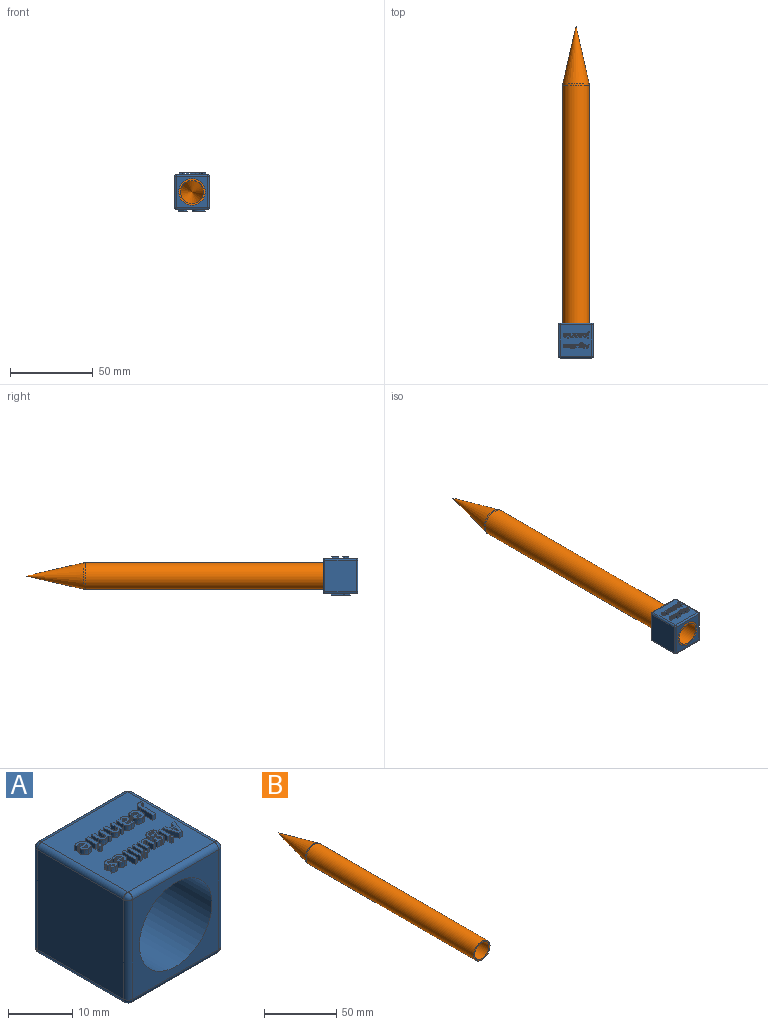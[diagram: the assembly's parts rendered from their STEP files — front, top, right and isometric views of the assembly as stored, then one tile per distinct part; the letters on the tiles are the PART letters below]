
ASSEMBLY  parts=2 mates=1
PART A: 354 faces, bbox 21x21x23 mm
  f0: plane 19x19mm, normal (0,0,1), area 317.9mm2, adj f7,f8,f9,f10,f11,f12,f13,f14
  f1: plane 19x19mm, normal (0,0,-1), area 267.5mm2, adj f136,f140,f141,f142,f156,f157,f158,f159
  f2: plane 19x19mm, normal (-1,0,0), area 361mm2, adj f141,f150,f151,f155
  f3: plane 19x19mm, normal (1,0,0), area 361mm2, adj f136,f139,f143,f144
  f4: plane 19x19mm, normal (0,-1,0), area 159.9mm2, adj f6,f139,f140,f149,f150
  f5: plane 19x19mm, normal (0,1,0), area 159.9mm2, adj f6,f142,f143,f151,f152
  f6: cylinder r=8mm len=21mm, axis (0,-1,0), area 1055.6mm2, adj f4,f5
  f7: extruded ~1x0.37mm, area 0.4mm2, adj f0,f8,f16,f17
  f8: extruded ~1x0.71mm, area 0.8mm2, adj f0,f7,f9,f17
  f9: extruded ~1x0.8mm, area 0.8mm2, adj f0,f8,f10,f17
  f10: plane 2.79x1mm, normal (-1,0,0), area 2.8mm2, adj f0,f9,f11,f17
  f11: plane 1x0.63mm, normal (0,-1,0), area 0.6mm2, adj f0,f10,f12,f17
  f12: plane 2.79x1mm, normal (1,0,0), area 2.8mm2, adj f0,f11,f13,f17
  f13: extruded ~1x0.4mm, area 0.4mm2, adj f0,f12,f14,f17
  f14: extruded ~1x0.3mm, area 0.3mm2, adj f0,f13,f15,f17
  f15: extruded ~1x0.3mm, area 0.3mm2, adj f0,f14,f16,f17
  f16: plane 1x0.53mm, normal (1,0,0), area 0.5mm2, adj f0,f7,f15,f17
  f17: plane 3.86x1.32mm, normal (0,0,1), area 2.7mm2, adj f7,f8,f9,f10,f11,f12,f13,f14
  f18: extruded ~1x0.86mm, area 0.9mm2, adj f0,f19,f37,f38
  f19: extruded ~1x0.45mm, area 0.5mm2, adj f0,f18,f20,f38
  f20: extruded ~1x0.35mm, area 0.4mm2, adj f0,f19,f21,f38
  f21: plane 1x0.48mm, normal (-1,0,0), area 0.5mm2, adj f0,f20,f22,f38
  f22: extruded ~1x0.38mm, area 0.4mm2, adj f0,f21,f23,f38
  f23: extruded ~1x0.39mm, area 0.4mm2, adj f0,f22,f24,f38
  f24: extruded ~1x0.41mm, area 0.4mm2, adj f0,f23,f25,f38
  f25: extruded ~1x0.41mm, area 0.5mm2, adj f0,f24,f26,f38
  f26: plane 1.47x1mm, normal (0,1,0), area 1.5mm2, adj f0,f25,f27,f38
  f27: plane 1x0.3mm, normal (-1,0,0), area 0.3mm2, adj f0,f26,f28,f38
  f28: extruded ~1x0.76mm, area 0.8mm2, adj f0,f27,f29,f38
  f29: extruded ~1x0.75mm, area 0.8mm2, adj f0,f28,f30,f38
  f30: extruded ~1x0.79mm, area 0.9mm2, adj f0,f29,f31,f38
  f31: extruded ~1x0.89mm, area 1mm2, adj f0,f30,f37,f38
  f32: extruded ~1x0.31mm, area 0.3mm2, adj f33,f36,f38,f39
  f33: extruded ~1x0.31mm, area 0.3mm2, adj f32,f34,f38,f39
  f34: extruded ~1x0.36mm, area 0.4mm2, adj f33,f35,f38,f39
  f35: plane 1x0.87mm, normal (0,-1,0), area 0.9mm2, adj f34,f36,f38,f39
  f36: extruded ~1x0.36mm, area 0.4mm2, adj f32,f35,f38,f39
  f37: extruded ~1x0.86mm, area 0.9mm2, adj f0,f18,f31,f38
  f38: plane 2.36x2.1mm, normal (0,0,1), area 3.1mm2, adj f18,f19,f20,f21,f22,f23,f24,f25
  f39: plane 0.87x0.48mm, normal (0,0,1), area 0.3mm2, adj f32,f33,f34,f35,f36
  f40: plane 1x0.24mm, normal (-0.04,1,0), area 0.2mm2, adj f41,f64,f65,f66
  f41: plane 1x0.19mm, normal (1,0,0), area 0.2mm2, adj f40,f42,f65,f66
  f42: extruded ~1x0.33mm, area 0.4mm2, adj f41,f43,f65,f66
  f43: extruded ~1x0.35mm, area 0.4mm2, adj f42,f44,f65,f66
  f44: extruded ~1x0.3mm, area 0.5mm2, adj f43,f45,f65,f66
  f45: extruded ~1x0.27mm, area 0.3mm2, adj f44,f64,f65,f66
  f46: plane 1x0.31mm, normal (0.93,0.36,0), area 0.3mm2, adj f0,f47,f63,f65
  f47: plane 1x0.43mm, normal (0,1,0), area 0.4mm2, adj f0,f46,f48,f65
  f48: plane 1.52x1mm, normal (-1,0,0), area 1.5mm2, adj f0,f47,f49,f65
  f49: extruded ~1x0.61mm, area 0.7mm2, adj f0,f48,f50,f65
  f50: extruded ~1x0.7mm, area 0.7mm2, adj f0,f49,f51,f65
  f51: extruded ~1x0.87mm, area 0.9mm2, adj f0,f50,f52,f65
  f52: plane 1x0.42mm, normal (0.9,0.44,0), area 0.5mm2, adj f0,f51,f53,f65
  f53: extruded ~1x0.64mm, area 0.7mm2, adj f0,f52,f54,f65
  f54: extruded ~1x0.36mm, area 0.6mm2, adj f0,f53,f55,f65
  f55: plane 1x0.1mm, normal (1,0,0), area 0.1mm2, adj f0,f54,f56,f65
  f56: plane 1x0.4mm, normal (0.03,-1,0), area 0.4mm2, adj f0,f55,f57,f65
  f57: extruded ~1x0.77mm, area 0.8mm2, adj f0,f56,f58,f65
  f58: extruded ~1x0.54mm, area 0.6mm2, adj f0,f57,f59,f65
  f59: extruded ~1x0.53mm, area 0.6mm2, adj f0,f58,f60,f65
  f60: extruded ~1x0.52mm, area 0.6mm2, adj f0,f59,f61,f65
  f61: extruded ~1x0.43mm, area 0.4mm2, adj f0,f60,f62,f65
  f62: extruded ~1x0.32mm, area 0.4mm2, adj f0,f61,f63,f65
  f63: plane 1x0.02mm, normal (0,1,0), area 0mm2, adj f0,f46,f62,f65
  f64: extruded ~1x0.4mm, area 0.4mm2, adj f40,f45,f65,f66
  f65: plane 2.37x2.03mm, normal (0,0,1), area 3.2mm2, adj f40,f41,f42,f43,f44,f45,f46,f47
  f66: plane 0.78x0.64mm, normal (0,0,1), area 0.4mm2, adj f40,f41,f42,f43,f44,f45,f64
  f67: plane 1x0.62mm, normal (0,1,0), area 0.6mm2, adj f0,f68,f83,f84
  f68: plane 1.49x1mm, normal (-1,0,0), area 1.5mm2, adj f0,f67,f69,f84
  f69: extruded ~1x0.62mm, area 0.7mm2, adj f0,f68,f70,f84
  f70: extruded ~1x0.6mm, area 0.7mm2, adj f0,f69,f71,f84
  f71: extruded ~1x0.41mm, area 0.4mm2, adj f0,f70,f72,f84
  f72: extruded ~1x0.29mm, area 0.4mm2, adj f0,f71,f73,f84
  f73: plane 1x0.03mm, normal (0,-1,0), area 0mm2, adj f0,f72,f74,f84
  f74: plane 1x0.29mm, normal (-0.96,-0.28,0), area 0.3mm2, adj f0,f73,f75,f84
  f75: plane 1x0.48mm, normal (0,-1,0), area 0.5mm2, adj f0,f74,f76,f84
  f76: plane 2.28x1mm, normal (1,0,0), area 2.3mm2, adj f0,f75,f77,f84
  f77: plane 1x0.62mm, normal (0,1,0), area 0.6mm2, adj f0,f76,f78,f84
  f78: plane 1.07x1mm, normal (-1,0,0), area 1.1mm2, adj f0,f77,f79,f84
  f79: extruded ~1x0.58mm, area 0.6mm2, adj f0,f78,f80,f84
  f80: extruded ~1x0.38mm, area 0.4mm2, adj f0,f79,f81,f84
  f81: extruded ~1x0.28mm, area 0.3mm2, adj f0,f80,f82,f84
  f82: extruded ~1x0.37mm, area 0.4mm2, adj f0,f81,f83,f84
  f83: plane 1.33x1mm, normal (1,0,0), area 1.3mm2, adj f0,f67,f82,f84
  f84: plane 2.32x2.1mm, normal (0,0,1), area 3.2mm2, adj f67,f68,f69,f70,f71,f72,f73,f74
  f85: plane 1x0.62mm, normal (0,1,0), area 0.6mm2, adj f0,f86,f101,f102
  f86: plane 1.49x1mm, normal (-1,0,0), area 1.5mm2, adj f0,f85,f87,f102
  f87: extruded ~1x0.62mm, area 0.7mm2, adj f0,f86,f88,f102
  f88: extruded ~1x0.6mm, area 0.7mm2, adj f0,f87,f89,f102
  f89: extruded ~1x0.41mm, area 0.4mm2, adj f0,f88,f90,f102
  f90: extruded ~1x0.29mm, area 0.4mm2, adj f0,f89,f91,f102
  f91: plane 1x0.03mm, normal (0,-1,0), area 0mm2, adj f0,f90,f92,f102
  f92: plane 1x0.29mm, normal (-0.96,-0.28,0), area 0.3mm2, adj f0,f91,f93,f102
  f93: plane 1x0.48mm, normal (0,-1,0), area 0.5mm2, adj f0,f92,f94,f102
  f94: plane 2.28x1mm, normal (1,0,0), area 2.3mm2, adj f0,f93,f95,f102
  f95: plane 1x0.62mm, normal (0,1,0), area 0.6mm2, adj f0,f94,f96,f102
  f96: plane 1.07x1mm, normal (-1,0,0), area 1.1mm2, adj f0,f95,f97,f102
  f97: extruded ~1x0.58mm, area 0.6mm2, adj f0,f96,f98,f102
  f98: extruded ~1x0.38mm, area 0.4mm2, adj f0,f97,f99,f102
  f99: extruded ~1x0.28mm, area 0.3mm2, adj f0,f98,f100,f102
  f100: extruded ~1x0.37mm, area 0.4mm2, adj f0,f99,f101,f102
  f101: plane 1.33x1mm, normal (1,0,0), area 1.3mm2, adj f0,f85,f100,f102
  f102: plane 2.32x2.1mm, normal (0,0,1), area 3.2mm2, adj f85,f86,f87,f88,f89,f90,f91,f92
  f103: extruded ~1x0.34mm, area 0.5mm2, adj f0,f104,f107,f108
  f104: extruded ~1x0.34mm, area 0.5mm2, adj f0,f103,f105,f108
  f105: extruded ~1x0.25mm, area 0.3mm2, adj f0,f104,f106,f108
  f106: extruded ~1x0.23mm, area 0.2mm2, adj f0,f105,f107,f108
  f107: extruded ~1x0.34mm, area 0.5mm2, adj f0,f103,f106,f108
  f108: plane 0.68x0.61mm, normal (0,0,1), area 0.3mm2, adj f103,f104,f105,f106,f107
  f109: plane 1x0.62mm, normal (0,1,0), area 0.6mm2, adj f0,f110,f112,f113
  f110: plane 2.28x1mm, normal (-1,0,0), area 2.3mm2, adj f0,f109,f111,f113
  f111: plane 1x0.62mm, normal (0,-1,0), area 0.6mm2, adj f0,f110,f112,f113
  f112: plane 2.28x1mm, normal (1,0,0), area 2.3mm2, adj f0,f109,f111,f113
  f113: plane 2.28x0.62mm, normal (0,0,1), area 1.4mm2, adj f109,f110,f111,f112
  f114: extruded ~1x0.86mm, area 0.9mm2, adj f0,f115,f133,f134
  f115: extruded ~1x0.45mm, area 0.5mm2, adj f0,f114,f116,f134
  f116: extruded ~1x0.35mm, area 0.4mm2, adj f0,f115,f117,f134
  f117: plane 1x0.48mm, normal (-1,0,0), area 0.5mm2, adj f0,f116,f118,f134
  f118: extruded ~1x0.38mm, area 0.4mm2, adj f0,f117,f119,f134
  f119: extruded ~1x0.39mm, area 0.4mm2, adj f0,f118,f120,f134
  f120: extruded ~1x0.41mm, area 0.4mm2, adj f0,f119,f121,f134
  f121: extruded ~1x0.41mm, area 0.5mm2, adj f0,f120,f122,f134
  f122: plane 1.47x1mm, normal (0,1,0), area 1.5mm2, adj f0,f121,f123,f134
  f123: plane 1x0.3mm, normal (-1,0,0), area 0.3mm2, adj f0,f122,f124,f134
  f124: extruded ~1x0.76mm, area 0.8mm2, adj f0,f123,f125,f134
  f125: extruded ~1x0.75mm, area 0.8mm2, adj f0,f124,f126,f134
  f126: extruded ~1x0.79mm, area 0.9mm2, adj f0,f125,f127,f134
  f127: extruded ~1x0.89mm, area 1mm2, adj f0,f126,f133,f134
  f128: extruded ~1x0.31mm, area 0.3mm2, adj f129,f132,f134,f135
  f129: extruded ~1x0.31mm, area 0.3mm2, adj f128,f130,f134,f135
  f130: extruded ~1x0.36mm, area 0.4mm2, adj f129,f131,f134,f135
  f131: plane 1x0.87mm, normal (0,-1,0), area 0.9mm2, adj f130,f132,f134,f135
  f132: extruded ~1x0.36mm, area 0.4mm2, adj f128,f131,f134,f135
  f133: extruded ~1x0.86mm, area 0.9mm2, adj f0,f114,f127,f134
  f134: plane 2.36x2.1mm, normal (0,0,1), area 3.1mm2, adj f114,f115,f116,f117,f118,f119,f120,f121
  f135: plane 0.87x0.48mm, normal (0,0,1), area 0.3mm2, adj f128,f129,f130,f131,f132
  f136: cylinder r=1mm len=19mm, axis (0,-1,0), area 29.8mm2, adj f1,f3,f137,f138
  f137: sphere r=1mm, area 1.6mm2, adj f136,f139,f140
  f138: sphere r=1mm, area 1.6mm2, adj f136,f142,f143
  f139: cylinder r=1mm len=19mm, axis (0,0,-1), area 29.8mm2, adj f3,f4,f137,f145
  f140: cylinder r=1mm len=19mm, axis (-1,0,0), area 29.8mm2, adj f1,f4,f137,f146
  f141: cylinder r=1mm len=19mm, axis (0,1,0), area 29.8mm2, adj f1,f2,f146,f147
  f142: cylinder r=1mm len=19mm, axis (1,0,0), area 29.8mm2, adj f1,f5,f138,f147
  f143: cylinder r=1mm len=19mm, axis (0,0,1), area 29.8mm2, adj f3,f5,f138,f148
  f144: cylinder r=1mm len=19mm, axis (0,1,0), area 29.8mm2, adj f0,f3,f145,f148
  f145: sphere r=1mm, area 1.6mm2, adj f139,f144,f149
  f146: sphere r=1mm, area 1.6mm2, adj f140,f141,f150
  f147: sphere r=1mm, area 1.6mm2, adj f141,f142,f151
  f148: sphere r=1mm, area 1.6mm2, adj f143,f144,f152
  f149: cylinder r=1mm len=19mm, axis (1,0,0), area 29.8mm2, adj f0,f4,f145,f153
  f150: cylinder r=1mm len=19mm, axis (0,0,1), area 29.8mm2, adj f2,f4,f146,f153
  f151: cylinder r=1mm len=19mm, axis (0,0,-1), area 29.8mm2, adj f2,f5,f147,f154
  f152: cylinder r=1mm len=19mm, axis (-1,0,0), area 29.8mm2, adj f0,f5,f148,f154
  f153: sphere r=1mm, area 1.6mm2, adj f149,f150,f155
  f154: sphere r=1mm, area 1.6mm2, adj f151,f152,f155
  f155: cylinder r=1mm len=19mm, axis (0,-1,0), area 29.8mm2, adj f0,f2,f153,f154
  f156: plane 2.34x1mm, normal (0,1,0), area 2.3mm2, adj f1,f157,f165,f166
  f157: plane 11.07x1mm, normal (1,0,0), area 11.1mm2, adj f1,f156,f158,f166
  f158: plane 1.92x1mm, normal (0,-1,0), area 1.9mm2, adj f1,f157,f159,f166
  f159: plane 3.57x2.84mm, normal (-0.62,-0.78,0), area 4.6mm2, adj f1,f158,f160,f166
  f160: plane 1.41x1.13mm, normal (-0.78,0.63,0), area 1.8mm2, adj f1,f159,f161,f166
  f161: plane 1.27x1.02mm, normal (0.63,0.78,0), area 1.6mm2, adj f1,f160,f162,f166
  f162: extruded ~1x0.81mm, area 1.1mm2, adj f1,f161,f163,f166
  f163: plane 1.15x1mm, normal (-1,-0.03,0), area 1.2mm2, adj f1,f162,f164,f166
  f164: plane 1.05x1mm, normal (-1,-0.02,0), area 1.1mm2, adj f1,f163,f165,f166
  f165: plane 6.41x1mm, normal (-1,0,0), area 6.4mm2, adj f1,f156,f164,f166
  f166: plane 11.07x5.49mm, normal (0,0,-1), area 31.7mm2, adj f156,f157,f158,f159,f160,f161,f162,f163
  f167: extruded ~1.15x1mm, area 1.3mm2, adj f168,f191,f192,f193
  f168: extruded ~1.2x1mm, area 1.4mm2, adj f167,f169,f192,f193
  f169: extruded ~1.52x1mm, area 1.6mm2, adj f168,f170,f192,f193
  f170: extruded ~1.07x1mm, area 1.2mm2, adj f169,f171,f192,f193
  f171: extruded ~1.22x1mm, area 1.3mm2, adj f170,f172,f192,f193
  f172: extruded ~1.13x1mm, area 1.3mm2, adj f171,f173,f192,f193
  f173: extruded ~1.28x1mm, area 1.4mm2, adj f172,f191,f192,f193
  f174: extruded ~4.89x1.39mm, area 5.2mm2, adj f1,f175,f190,f192
  f175: extruded ~2.63x1mm, area 2.7mm2, adj f1,f174,f176,f192
  f176: extruded ~1.66x1.41mm, area 2.2mm2, adj f1,f175,f177,f192
  f177: extruded ~2.14x1mm, area 2.2mm2, adj f1,f176,f178,f192
  f178: extruded ~2.77x1.03mm, area 3mm2, adj f1,f177,f179,f192
  f179: extruded ~2.81x1mm, area 3.1mm2, adj f1,f178,f180,f192
  f180: extruded ~2.57x1mm, area 2.8mm2, adj f1,f179,f181,f192
  f181: extruded ~2.32x1mm, area 2.6mm2, adj f1,f180,f182,f192
  f182: extruded ~2.4x1.29mm, area 2.9mm2, adj f1,f181,f183,f192
  f183: plane 1x0.1mm, normal (0,-1,0), area 0.1mm2, adj f1,f182,f184,f192
  f184: extruded ~2.02x1mm, area 2.1mm2, adj f1,f183,f185,f192
  f185: extruded ~1.14x1.08mm, area 1.6mm2, adj f1,f184,f186,f192
  f186: extruded ~1.97x1mm, area 2mm2, adj f1,f185,f187,f192
  f187: extruded ~1.33x1mm, area 1.3mm2, adj f1,f186,f188,f192
  f188: plane 1.87x1mm, normal (1,0,0), area 1.9mm2, adj f1,f187,f189,f192
  f189: extruded ~1.48x1mm, area 1.5mm2, adj f1,f188,f190,f192
  f190: extruded ~4.16x1.61mm, area 4.6mm2, adj f1,f174,f189,f192
  f191: extruded ~1.43x1mm, area 1.5mm2, adj f167,f173,f192,f193
  f192: plane 11.35x7.82mm, normal (0,0,-1), area 52.2mm2, adj f167,f168,f169,f170,f171,f172,f173,f174
  f193: plane 3.68x3.23mm, normal (0,0,-1), area 9.6mm2, adj f167,f168,f169,f170,f171,f172,f173,f191
  f194: extruded ~1x0.98mm, area 1mm2, adj f195,f205,f206,f207
  f195: plane 1x0.7mm, normal (0,-1,0), area 0.7mm2, adj f194,f196,f206,f207
  f196: extruded ~1.16x1mm, area 1.2mm2, adj f195,f205,f206,f207
  f197: plane 1x0.64mm, normal (0.96,0.29,0), area 0.7mm2, adj f0,f198,f204,f206
  f198: plane 1x0.61mm, normal (0,1,0), area 0.6mm2, adj f0,f197,f199,f206
  f199: plane 2.7x1mm, normal (-0.94,-0.33,0), area 2.9mm2, adj f0,f198,f200,f206
  f200: plane 1x0.7mm, normal (0,-1,0), area 0.7mm2, adj f0,f199,f201,f206
  f201: plane 2.7x1mm, normal (0.94,-0.33,0), area 2.9mm2, adj f0,f200,f202,f206
  f202: plane 1x0.61mm, normal (0,1,0), area 0.6mm2, adj f0,f201,f203,f206
  f203: plane 1x0.64mm, normal (-0.96,0.29,0), area 0.7mm2, adj f0,f202,f204,f206
  f204: plane 1x0.98mm, normal (0,1,0), area 1mm2, adj f0,f197,f203,f206
  f205: extruded ~1x0.18mm, area 0.2mm2, adj f194,f196,f206,f207
  f206: plane 2.7x2.6mm, normal (0,0,1), area 3.3mm2, adj f194,f195,f196,f197,f198,f199,f200,f201
  f207: plane 1.16x0.7mm, normal (0,0,1), area 0.4mm2, adj f194,f195,f196,f205
  f208: extruded ~1x0.31mm, area 0.5mm2, adj f0,f209,f212,f213
  f209: extruded ~1x0.31mm, area 0.5mm2, adj f0,f208,f210,f213
  f210: extruded ~1x0.23mm, area 0.2mm2, adj f0,f209,f211,f213
  f211: extruded ~1x0.2mm, area 0.2mm2, adj f0,f210,f212,f213
  f212: extruded ~1x0.31mm, area 0.5mm2, adj f0,f208,f211,f213
  f213: plane 0.61x0.55mm, normal (0,0,1), area 0.3mm2, adj f208,f209,f210,f211,f212
  f214: plane 1x0.56mm, normal (0,1,0), area 0.6mm2, adj f0,f215,f217,f218
  f215: plane 2.06x1mm, normal (-1,0,0), area 2.1mm2, adj f0,f214,f216,f218
  f216: plane 1x0.56mm, normal (0,-1,0), area 0.6mm2, adj f0,f215,f217,f218
  f217: plane 2.06x1mm, normal (1,0,0), area 2.1mm2, adj f0,f214,f216,f218
  f218: plane 2.06x0.56mm, normal (0,0,1), area 1.2mm2, adj f214,f215,f216,f217
  f219: extruded ~1x0.27mm, area 0.3mm2, adj f220,f262,f263,f264
  f220: extruded ~1x0.37mm, area 0.6mm2, adj f219,f221,f263,f264
  f221: extruded ~1x0.37mm, area 0.5mm2, adj f220,f222,f263,f264
  f222: extruded ~1x0.27mm, area 0.3mm2, adj f221,f223,f263,f264
  f223: extruded ~1x0.23mm, area 0.3mm2, adj f222,f262,f263,f264
  f224: extruded ~1x0.18mm, area 0.2mm2, adj f225,f260,f263,f265
  f225: extruded ~1x0.19mm, area 0.2mm2, adj f224,f226,f263,f265
  f226: extruded ~1x0.26mm, area 0.3mm2, adj f225,f227,f263,f265
  f227: plane 1x0.29mm, normal (0,1,0), area 0.3mm2, adj f226,f228,f263,f265
  f228: extruded ~1x0.31mm, area 0.3mm2, adj f227,f229,f263,f265
  f229: extruded ~1x0.16mm, area 0.2mm2, adj f228,f230,f263,f265
  f230: extruded ~1x0.23mm, area 0.3mm2, adj f229,f231,f263,f265
  f231: extruded ~1x0.47mm, area 0.5mm2, adj f230,f260,f263,f265
  f232: plane 1x0.29mm, normal (-1,0,0), area 0.3mm2, adj f0,f233,f261,f263
  f233: plane 1x0.72mm, normal (0,-1,0), area 0.7mm2, adj f0,f232,f234,f263
  f234: extruded ~1x0.15mm, area 0.2mm2, adj f0,f233,f235,f263
  f235: extruded ~1x0.21mm, area 0.2mm2, adj f0,f234,f236,f263
  f236: extruded ~1x0.63mm, area 0.7mm2, adj f0,f235,f237,f263
  f237: extruded ~1x0.52mm, area 0.6mm2, adj f0,f236,f238,f263
  f238: extruded ~1x0.36mm, area 0.4mm2, adj f0,f237,f239,f263
  f239: extruded ~1x0.26mm, area 0.3mm2, adj f0,f238,f240,f263
  f240: extruded ~1x0.2mm, area 0.3mm2, adj f0,f239,f241,f263
  f241: extruded ~1x0.2mm, area 0.2mm2, adj f0,f240,f242,f263
  f242: extruded ~1x0.18mm, area 0.2mm2, adj f0,f241,f243,f263
  f243: extruded ~1x0.15mm, area 0.2mm2, adj f0,f242,f244,f263
  f244: extruded ~1x0.34mm, area 0.4mm2, adj f0,f243,f245,f263
  f245: extruded ~1x0.31mm, area 0.3mm2, adj f0,f244,f246,f263
  f246: extruded ~1x0.42mm, area 0.5mm2, adj f0,f245,f247,f263
  f247: extruded ~1x0.66mm, area 0.7mm2, adj f0,f246,f248,f263
  f248: extruded ~1x0.86mm, area 0.9mm2, adj f0,f247,f249,f263
  f249: extruded ~1x0.56mm, area 0.7mm2, adj f0,f248,f250,f263
  f250: extruded ~1x0.43mm, area 0.5mm2, adj f0,f249,f251,f263
  f251: extruded ~1x0.52mm, area 0.5mm2, adj f0,f250,f252,f263
  f252: plane 1x0.35mm, normal (0,-1,0), area 0.3mm2, adj f0,f251,f253,f263
  f253: extruded ~1x0.31mm, area 0.4mm2, adj f0,f252,f254,f263
  f254: extruded ~1x0.15mm, area 0.2mm2, adj f0,f253,f255,f263
  f255: plane 1x0.08mm, normal (0.11,0.99,0), area 0.1mm2, adj f0,f254,f256,f263
  f256: plane 1x0.1mm, normal (0.06,1,0), area 0.1mm2, adj f0,f255,f257,f263
  f257: extruded ~1x0.64mm, area 0.7mm2, adj f0,f256,f258,f263
  f258: extruded ~1x0.52mm, area 0.6mm2, adj f0,f257,f259,f263
  f259: extruded ~1x0.31mm, area 0.3mm2, adj f0,f258,f261,f263
  f260: extruded ~1x0.31mm, area 0.3mm2, adj f224,f231,f263,f265
  f261: plane 1x0.32mm, normal (-0.25,0.97,0), area 0.3mm2, adj f0,f232,f259,f263
  f262: extruded ~1x0.23mm, area 0.3mm2, adj f219,f223,f263,f264
  f263: plane 3x2.07mm, normal (0,0,1), area 3.7mm2, adj f219,f220,f221,f222,f223,f224,f225,f226
  f264: plane 0.73x0.61mm, normal (0,0,1), area 0.4mm2, adj f219,f220,f221,f222,f223,f262
  f265: plane 1.07x0.51mm, normal (0,0,1), area 0.5mm2, adj f224,f225,f226,f227,f228,f229,f230,f231
  f266: plane 1x0.26mm, normal (0.96,0.28,0), area 0.3mm2, adj f0,f267,f282,f283
  f267: plane 1x0.43mm, normal (0,1,0), area 0.4mm2, adj f0,f266,f268,f283
  f268: plane 2.06x1mm, normal (-1,0,0), area 2.1mm2, adj f0,f267,f269,f283
  f269: plane 1x0.56mm, normal (0,-1,0), area 0.6mm2, adj f0,f268,f270,f283
  f270: plane 1x0.97mm, normal (1,0,0), area 1mm2, adj f0,f269,f271,f283
  f271: extruded ~1x0.52mm, area 0.5mm2, adj f0,f270,f272,f283
  f272: extruded ~1x0.34mm, area 0.4mm2, adj f0,f271,f273,f283
  f273: extruded ~1x0.25mm, area 0.3mm2, adj f0,f272,f274,f283
  f274: extruded ~1x0.33mm, area 0.3mm2, adj f0,f273,f275,f283
  f275: plane 1.2x1mm, normal (-1,0,0), area 1.2mm2, adj f0,f274,f276,f283
  f276: plane 1x0.56mm, normal (0,-1,0), area 0.6mm2, adj f0,f275,f277,f283
  f277: plane 1.34x1mm, normal (1,0,0), area 1.3mm2, adj f0,f276,f278,f283
  f278: extruded ~1x0.56mm, area 0.6mm2, adj f0,f277,f279,f283
  f279: extruded ~1x0.55mm, area 0.6mm2, adj f0,f278,f280,f283
  f280: extruded ~1x0.38mm, area 0.4mm2, adj f0,f279,f281,f283
  f281: extruded ~1x0.26mm, area 0.3mm2, adj f0,f280,f282,f283
  f282: plane 1x0.03mm, normal (0,1,0), area 0mm2, adj f0,f266,f281,f283
  f283: plane 2.09x1.9mm, normal (0,0,1), area 2.6mm2, adj f266,f267,f268,f269,f270,f271,f272,f273
  f284: extruded ~1x0.31mm, area 0.5mm2, adj f0,f285,f288,f289
  f285: extruded ~1x0.31mm, area 0.5mm2, adj f0,f284,f286,f289
  f286: extruded ~1x0.23mm, area 0.2mm2, adj f0,f285,f287,f289
  f287: extruded ~1x0.2mm, area 0.2mm2, adj f0,f286,f288,f289
  f288: extruded ~1x0.31mm, area 0.5mm2, adj f0,f284,f287,f289
  f289: plane 0.61x0.55mm, normal (0,0,1), area 0.3mm2, adj f284,f285,f286,f287,f288
  f290: plane 1x0.56mm, normal (0,1,0), area 0.6mm2, adj f0,f291,f293,f294
  f291: plane 2.06x1mm, normal (-1,0,0), area 2.1mm2, adj f0,f290,f292,f294
  f292: plane 1x0.56mm, normal (0,-1,0), area 0.6mm2, adj f0,f291,f293,f294
  f293: plane 2.06x1mm, normal (1,0,0), area 2.1mm2, adj f0,f290,f292,f294
  f294: plane 2.06x0.56mm, normal (0,0,1), area 1.2mm2, adj f290,f291,f292,f293
  f295: plane 1x0.56mm, normal (0,1,0), area 0.6mm2, adj f0,f296,f298,f299
  f296: plane 2.86x1mm, normal (-1,0,0), area 2.9mm2, adj f0,f295,f297,f299
  f297: plane 1x0.56mm, normal (0,-1,0), area 0.6mm2, adj f0,f296,f298,f299
  f298: plane 2.86x1mm, normal (1,0,0), area 2.9mm2, adj f0,f295,f297,f299
  f299: plane 2.86x0.56mm, normal (0,0,1), area 1.6mm2, adj f295,f296,f297,f298
  f300: plane 1x0.56mm, normal (0,1,0), area 0.6mm2, adj f0,f301,f303,f304
  f301: plane 2.86x1mm, normal (-1,0,0), area 2.9mm2, adj f0,f300,f302,f304
  f302: plane 1x0.56mm, normal (0,-1,0), area 0.6mm2, adj f0,f301,f303,f304
  f303: plane 2.86x1mm, normal (1,0,0), area 2.9mm2, adj f0,f300,f302,f304
  f304: plane 2.86x0.56mm, normal (0,0,1), area 1.6mm2, adj f300,f301,f302,f303
  f305: extruded ~1x0.78mm, area 0.8mm2, adj f0,f306,f324,f325
  f306: extruded ~1x0.41mm, area 0.4mm2, adj f0,f305,f307,f325
  f307: extruded ~1x0.31mm, area 0.3mm2, adj f0,f306,f308,f325
  f308: plane 1x0.43mm, normal (-1,0,0), area 0.4mm2, adj f0,f307,f309,f325
  f309: extruded ~1x0.35mm, area 0.4mm2, adj f0,f308,f310,f325
  f310: extruded ~1x0.35mm, area 0.4mm2, adj f0,f309,f311,f325
  f311: extruded ~1x0.37mm, area 0.4mm2, adj f0,f310,f312,f325
  f312: extruded ~1x0.37mm, area 0.4mm2, adj f0,f311,f313,f325
  f313: plane 1.33x1mm, normal (0,1,0), area 1.3mm2, adj f0,f312,f314,f325
  f314: plane 1x0.27mm, normal (-1,0,0), area 0.3mm2, adj f0,f313,f315,f325
  f315: extruded ~1x0.69mm, area 0.7mm2, adj f0,f314,f316,f325
  f316: extruded ~1x0.68mm, area 0.7mm2, adj f0,f315,f317,f325
  f317: extruded ~1x0.71mm, area 0.8mm2, adj f0,f316,f318,f325
  f318: extruded ~1x0.8mm, area 0.9mm2, adj f0,f317,f324,f325
  f319: extruded ~1x0.28mm, area 0.3mm2, adj f320,f323,f325,f326
  f320: extruded ~1x0.28mm, area 0.3mm2, adj f319,f321,f325,f326
  f321: extruded ~1x0.32mm, area 0.3mm2, adj f320,f322,f325,f326
  f322: plane 1x0.79mm, normal (0,-1,0), area 0.8mm2, adj f321,f323,f325,f326
  f323: extruded ~1x0.32mm, area 0.3mm2, adj f319,f322,f325,f326
  f324: extruded ~1x0.78mm, area 0.8mm2, adj f0,f305,f318,f325
  f325: plane 2.13x1.89mm, normal (0,0,1), area 2.6mm2, adj f305,f306,f307,f308,f309,f310,f311,f312
  f326: plane 0.79x0.43mm, normal (0,0,1), area 0.3mm2, adj f319,f320,f321,f322,f323
  f327: extruded ~1x0.48mm, area 0.6mm2, adj f0,f328,f352,f353
  f328: extruded ~1x0.26mm, area 0.3mm2, adj f0,f327,f329,f353
  f329: extruded ~1x0.2mm, area 0.3mm2, adj f0,f328,f330,f353
  f330: extruded ~1x0.35mm, area 0.4mm2, adj f0,f329,f331,f353
  f331: extruded ~1x0.35mm, area 0.4mm2, adj f0,f330,f332,f353
  f332: extruded ~1x0.13mm, area 0.2mm2, adj f0,f331,f333,f353
  f333: extruded ~1x0.25mm, area 0.3mm2, adj f0,f332,f334,f353
  f334: extruded ~1x0.27mm, area 0.3mm2, adj f0,f333,f335,f353
  f335: extruded ~1x0.29mm, area 0.3mm2, adj f0,f334,f336,f353
  f336: plane 1x0.4mm, normal (-0.92,0.39,0), area 0.4mm2, adj f0,f335,f337,f353
  f337: extruded ~1x0.72mm, area 0.7mm2, adj f0,f336,f338,f353
  f338: extruded ~1x0.6mm, area 0.6mm2, adj f0,f337,f339,f353
  f339: extruded ~1x0.42mm, area 0.5mm2, adj f0,f338,f340,f353
  f340: extruded ~1x0.27mm, area 0.3mm2, adj f0,f339,f341,f353
  f341: extruded ~1x0.19mm, area 0.3mm2, adj f0,f340,f342,f353
  f342: extruded ~1x0.35mm, area 0.4mm2, adj f0,f341,f343,f353
  f343: extruded ~1x0.26mm, area 0.3mm2, adj f0,f342,f344,f353
  f344: extruded ~1x0.14mm, area 0.2mm2, adj f0,f343,f345,f353
  f345: extruded ~1x0.11mm, area 0.1mm2, adj f0,f344,f346,f353
  f346: extruded ~1x0.31mm, area 0.4mm2, adj f0,f345,f347,f353
  f347: extruded ~1x0.35mm, area 0.3mm2, adj f0,f346,f348,f353
  f348: extruded ~1x0.35mm, area 0.4mm2, adj f0,f347,f349,f353
  f349: plane 1x0.46mm, normal (1,0,0), area 0.5mm2, adj f0,f348,f350,f353
  f350: extruded ~1x0.3mm, area 0.3mm2, adj f0,f349,f351,f353
  f351: extruded ~1x0.38mm, area 0.4mm2, adj f0,f350,f352,f353
  f352: extruded ~1x0.66mm, area 0.7mm2, adj f0,f327,f351,f353
  f353: plane 2.13x1.56mm, normal (0,0,1), area 2.1mm2, adj f327,f328,f329,f330,f331,f332,f333,f334
PART B: 8 faces, bbox 16x200x16 mm
  f0: cylinder r=7mm len=165mm, axis (0,1,0), area 7257.1mm2, adj f2,f4
  f1: cylinder r=8mm len=164.44mm, axis (0,1,0), area 8265.4mm2, adj f2,f5
  f2: plane 16x16mm, normal (0,-1,0), area 47.1mm2, adj f0,f1
  f3: cone r=8mm half-angle=12.9deg, axis (0,-1,0), area 874.2mm2, adj f5
  f4: plane 14x14mm, normal (0,-1,0), area 1.8mm2, adj f0,f6
  f5: torus R=3mm, axis (0,-1,0), area 56.2mm2, adj f1,f3
  f6: torus R=3mm, axis (0,-1,0), area 14.5mm2, adj f4,f7
  f7: cone r=7.03mm half-angle=12.9deg, axis (0,-1,0), area 671.1mm2, adj f6
PLACE A t=(-21.67,-2.37,-0.53)mm fixed
PLACE B t=(-21.67,141.63,-0.53)mm
MATE fastened B.f0 <-> A.f6  axis (0,1,0) through (-21.67,-23.37,-0.53)mm
